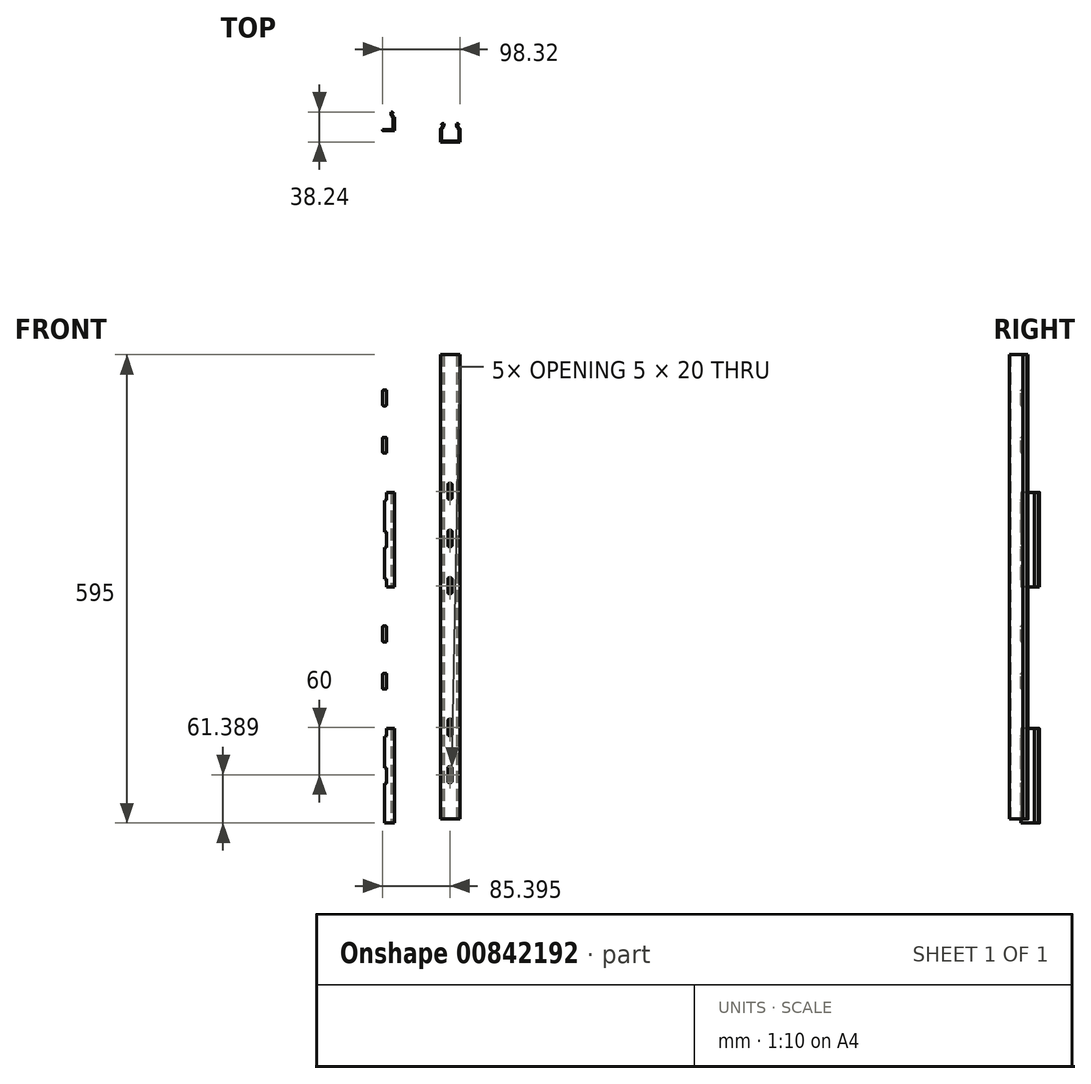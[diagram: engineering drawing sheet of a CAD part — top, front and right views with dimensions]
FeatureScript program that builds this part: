
annotation { "Feature Type Name" : "Feature", "Feature Type Description" : "" }
export const myFeature = defineFeature(function(context is Context, id is Id, definition is map)
    precondition{}
    {
        {
            var Q0;
            Q0=qCreatedBy(makeId("Top.planeOp"),FACE);
            var sketch = newSketch(context, id + "F0", { "sketchPlane" : qUnion([Q0])});
            skLineSegment(sketch, "E0", {"start": v(-70.87, 0) * mm, "end": v(-95.87, 0) * mm});
            skLineSegment(sketch, "E1", {"start": v(-95.87, 0) * mm, "end": v(-95.87, 17) * mm});
            skLineSegment(sketch, "E2", {"start": v(-83.37, 1.5) * mm, "end": v(-83.37, 14.96) * mm});
            skLineSegment(sketch, "E3", {"start": v(-94.37, 22) * mm, "end": v(-92.87, 22) * mm});
            skLineSegment(sketch, "E4.MirrorCS", {"start": v(-70.87, 0) * mm, "end": v(-70.87, 17) * mm});
            skPoint(sketch, "E5.orphan", {"position": v(-83.37, 0) * mm});
            skArc(sketch, "E6", {"start": v(-95.87, 17) * mm, "mid": v(-93.72, 19.11) * mm, "end": v(-92.87, 22) * mm});
            skLineSegment(sketch, "E7.1", {"start": v(-72.37, 1.5) * mm, "end": v(-72.37, 16.2) * mm});
            skLineSegment(sketch, "E7.2", {"start": v(-72.37, 1.5) * mm, "end": v(-94.37, 1.5) * mm});
            skLineSegment(sketch, "E7.3", {"start": v(-94.37, 1.5) * mm, "end": v(-94.37, 16.2) * mm});
            skArc(sketch, "E7.4", {"start": v(-94.37, 16.2) * mm, "mid": v(-91.9, 19.44) * mm, "end": v(-91.48, 23.5) * mm});
            skLineSegment(sketch, "E8.MirrorCS", {"start": v(-72.37, 22) * mm, "end": v(-73.87, 22) * mm});
            skArc(sketch, "E9.MirrorCS", {"start": v(-72.37, 16.2) * mm, "mid": v(-74.85, 19.44) * mm, "end": v(-75.26, 23.5) * mm});
            skArc(sketch, "E10.MirrorCS", {"start": v(-70.87, 17) * mm, "mid": v(-73.02, 19.11) * mm, "end": v(-73.87, 22) * mm});
            skArc(sketch, "E11", {"start": v(-91.48, 23.5) * mm, "mid": v(-93.28, 23.42) * mm, "end": v(-94.37, 22) * mm});
            skArc(sketch, "E12.MirrorCS", {"start": v(-75.26, 23.5) * mm, "mid": v(-73.47, 23.42) * mm, "end": v(-72.37, 22) * mm});
            skSolve(sketch);
        }
        {
            var Q0;
            {var subQ1=sQuery(id+"F0.wireOp",EDGE,"E0");Q0=makeQuery(id+"F0.imprint","IMPRINT",FACE,{"disambiguationData":[TD([[makeQuery(id+"F0.imprint","IMPRINT",EDGE,{"derivedFrom":subQ1}),-1.0]])]});}
            var Q1;
            Q1=makeQuery(id+"F0.imprint","IMPRINT",FACE,{"disambiguationData":[TD([[makeQuery(id+"F0.imprint","IMPRINT",EDGE,{"derivedFrom":sQuery(id+"F0.wireOp",EDGE,"8c0a88f1-b1bc-4309-b33d-9bf5d8da761c0.MirrorCS")}),-1.0]])]});
            var Q2;
            {var subQ5=sQuery(id+"F0.wireOp",EDGE,"E1");Q2=makeQuery(id+"F0.imprint","IMPRINT",FACE,{"disambiguationData":[TD([[makeQuery(id+"F0.imprint","IMPRINT",EDGE,{"derivedFrom":subQ5}),-1.0]])]});}
            var Q3;
            Q3=makeQuery(id+"F0.imprint","IMPRINT",FACE,{"disambiguationData":[TD([[makeQuery(id+"F0.imprint","IMPRINT",EDGE,{"derivedFrom":sQuery(id+"F0.wireOp",EDGE,"33b4dc04-297a-427e-952f-5a77545de1140.MirrorCS")}),-1.0]])]});
            extrude(context, id + "F1", {"entities" : qUnion([Q0, Q1, Q2, Q3]), "endBound" : BoundingType.SYMMETRIC, "depth" : 600 * mm, "offsetDistance" : 25 * mm});
        }
        {
            var Q0;
            Q0=makeQuery(id+"F1.opExtrude","SWEPT_FACE",FACE,{"disambiguationData":[OSD([sQuery(id+"F0.wireOp",EDGE,"E0")])]});
            var sketch = newSketch(context, id + "F2", { "sketchPlane" : qUnion([Q0])});
            skLineSegment(sketch, "E13", {"start": v(-83.37, -300) * mm, "end": v(-83.37, 300) * mm});
            skLineSegment(sketch, "E14.bottom", {"start": v(-81.87, 10) * mm, "end": v(-84.87, 10) * mm});
            skLineSegment(sketch, "E14.top", {"start": v(-81.87, -10) * mm, "end": v(-84.87, -10) * mm});
            skLineSegment(sketch, "E14.left", {"start": v(-80.87, 9) * mm, "end": v(-80.87, -9) * mm});
            skLineSegment(sketch, "E14.right", {"start": v(-85.87, 9) * mm, "end": v(-85.87, -9) * mm});
            skPoint(sketch, "E14.middle", {"position": v(-83.37, 0) * mm});
            skPoint(sketch, "E15.visualSharp", {"position": v(-85.87, -10) * mm});
            skArc(sketch, "E15.filletArc", {"start": v(-85.87, -9) * mm, "mid": v(-85.58, -9.7) * mm, "end": v(-84.87, -10) * mm});
            skPoint(sketch, "E16.visualSharp", {"position": v(-80.87, -10) * mm});
            skArc(sketch, "E16.filletArc", {"start": v(-81.87, -10) * mm, "mid": v(-81.16, -9.7) * mm, "end": v(-80.87, -9) * mm});
            skPoint(sketch, "E17.visualSharp", {"position": v(-85.87, 10) * mm});
            skArc(sketch, "E17.filletArc", {"start": v(-84.87, 10) * mm, "mid": v(-85.58, 9.7) * mm, "end": v(-85.87, 9) * mm});
            skPoint(sketch, "E18.visualSharp", {"position": v(-80.87, 10) * mm});
            skArc(sketch, "E18.filletArc", {"start": v(-80.87, 9) * mm, "mid": v(-81.16, 9.7) * mm, "end": v(-81.87, 10) * mm});
            skLineSegment(sketch, "E19.MirrorCS", {"start": v(-80.87, -69) * mm, "end": v(-80.87, -51) * mm});
            skLineSegment(sketch, "E20.MirrorCS", {"start": v(-81.87, -70) * mm, "end": v(-84.87, -70) * mm});
            skArc(sketch, "E21.MirrorCS", {"start": v(-80.87, -69) * mm, "mid": v(-81.16, -69.7) * mm, "end": v(-81.87, -70) * mm});
            skArc(sketch, "E22.MirrorCS", {"start": v(-84.87, -70) * mm, "mid": v(-85.58, -69.7) * mm, "end": v(-85.87, -69) * mm});
            skLineSegment(sketch, "E23.MirrorCS", {"start": v(-85.87, -69) * mm, "end": v(-85.87, -51) * mm});
            skArc(sketch, "E24.MirrorCS", {"start": v(-85.87, -51) * mm, "mid": v(-85.58, -50.3) * mm, "end": v(-84.87, -50) * mm});
            skLineSegment(sketch, "E25.MirrorCS", {"start": v(-81.87, -50) * mm, "end": v(-84.87, -50) * mm});
            skArc(sketch, "E26.MirrorCS", {"start": v(-81.87, -50) * mm, "mid": v(-81.16, -50.3) * mm, "end": v(-80.87, -51) * mm});
            skLineSegment(sketch, "E27", {"start": v(-83.37, 0) * mm, "end": v(-70.87, 0) * mm});
            skArc(sketch, "E28.MirrorCS", {"start": v(-84.87, 70) * mm, "mid": v(-85.58, 69.7) * mm, "end": v(-85.87, 69) * mm});
            skArc(sketch, "E29.MirrorCS", {"start": v(-85.87, 51) * mm, "mid": v(-85.58, 50.3) * mm, "end": v(-84.87, 50) * mm});
            skArc(sketch, "E30.MirrorCS", {"start": v(-80.87, 69) * mm, "mid": v(-81.16, 69.7) * mm, "end": v(-81.87, 70) * mm});
            skArc(sketch, "E31.MirrorCS", {"start": v(-81.87, 50) * mm, "mid": v(-81.16, 50.3) * mm, "end": v(-80.87, 51) * mm});
            skLineSegment(sketch, "E32.MirrorCS", {"start": v(-85.87, 69) * mm, "end": v(-85.87, 51) * mm});
            skLineSegment(sketch, "E33.MirrorCS", {"start": v(-81.87, 70) * mm, "end": v(-84.87, 70) * mm});
            skLineSegment(sketch, "E34.MirrorCS", {"start": v(-80.87, 69) * mm, "end": v(-80.87, 51) * mm});
            skLineSegment(sketch, "E35.MirrorCS", {"start": v(-81.87, 50) * mm, "end": v(-84.87, 50) * mm});
            skLineSegment(sketch, "E36", {"start": v(-83.37, -10) * mm, "end": v(-83.37, -50) * mm});
            skLineSegment(sketch, "E37", {"start": v(-85.87, -60) * mm, "end": v(-70.87, -60) * mm});
            skArc(sketch, "E38.MirrorCS", {"start": v(-81.87, -110) * mm, "mid": v(-81.16, -110.3) * mm, "end": v(-80.87, -111) * mm});
            skArc(sketch, "E39.MirrorCS", {"start": v(-84.87, -130) * mm, "mid": v(-85.58, -129.7) * mm, "end": v(-85.87, -129) * mm});
            skLineSegment(sketch, "E40.MirrorCS", {"start": v(-81.87, -110) * mm, "end": v(-84.87, -110) * mm});
            skArc(sketch, "E41.MirrorCS", {"start": v(-80.87, -129) * mm, "mid": v(-81.16, -129.7) * mm, "end": v(-81.87, -130) * mm});
            skLineSegment(sketch, "E42.MirrorCS", {"start": v(-81.87, -130) * mm, "end": v(-84.87, -130) * mm});
            skArc(sketch, "E43.MirrorCS", {"start": v(-85.87, -111) * mm, "mid": v(-85.58, -110.3) * mm, "end": v(-84.87, -110) * mm});
            skPoint(sketch, "E44.MirrorP", {"position": v(-80.87, -130) * mm});
            skPoint(sketch, "E45.MirrorP", {"position": v(-80.87, -110) * mm});
            skPoint(sketch, "E46.MirrorP", {"position": v(-85.87, -110) * mm});
            skLineSegment(sketch, "E47.MirrorCS", {"start": v(-83.37, -120) * mm, "end": v(-70.87, -120) * mm});
            skLineSegment(sketch, "E48.MirrorCS", {"start": v(-80.87, -129) * mm, "end": v(-80.87, -111) * mm});
            skPoint(sketch, "E49.MirrorP", {"position": v(-85.87, -130) * mm});
            skLineSegment(sketch, "E50.MirrorCS", {"start": v(-85.87, -129) * mm, "end": v(-85.87, -111) * mm});
            skPoint(sketch, "E51.MirrorP", {"position": v(-83.37, -120) * mm});
            skLineSegment(sketch, "E52.MirrorCS", {"start": v(-81.87, -190) * mm, "end": v(-84.87, -190) * mm});
            skArc(sketch, "E53.MirrorCS", {"start": v(-84.87, -170) * mm, "mid": v(-85.58, -170.3) * mm, "end": v(-85.87, -171) * mm});
            skArc(sketch, "E54.MirrorCS", {"start": v(-80.87, -171) * mm, "mid": v(-81.16, -170.3) * mm, "end": v(-81.87, -170) * mm});
            skLineSegment(sketch, "E55.MirrorCS", {"start": v(-81.87, -170) * mm, "end": v(-84.87, -170) * mm});
            skArc(sketch, "E56.MirrorCS", {"start": v(-85.87, -189) * mm, "mid": v(-85.58, -189.7) * mm, "end": v(-84.87, -190) * mm});
            skArc(sketch, "E57.MirrorCS", {"start": v(-81.87, -190) * mm, "mid": v(-81.16, -189.7) * mm, "end": v(-80.87, -189) * mm});
            skLineSegment(sketch, "E58.MirrorCS", {"start": v(-80.87, -171) * mm, "end": v(-80.87, -189) * mm});
            skLineSegment(sketch, "E59.MirrorCS", {"start": v(-85.87, -180) * mm, "end": v(-70.87, -180) * mm});
            skLineSegment(sketch, "E60.MirrorCS", {"start": v(-85.87, -171) * mm, "end": v(-85.87, -189) * mm});
            skLineSegment(sketch, "E61.MirrorCS", {"start": v(-81.87, -250) * mm, "end": v(-84.87, -250) * mm});
            skArc(sketch, "E62.MirrorCS", {"start": v(-84.87, -230) * mm, "mid": v(-85.58, -230.3) * mm, "end": v(-85.87, -231) * mm});
            skArc(sketch, "E63.MirrorCS", {"start": v(-85.87, -249) * mm, "mid": v(-85.58, -249.7) * mm, "end": v(-84.87, -250) * mm});
            skLineSegment(sketch, "E64.MirrorCS", {"start": v(-81.87, -230) * mm, "end": v(-84.87, -230) * mm});
            skArc(sketch, "E65.MirrorCS", {"start": v(-80.87, -231) * mm, "mid": v(-81.16, -230.3) * mm, "end": v(-81.87, -230) * mm});
            skArc(sketch, "E66.MirrorCS", {"start": v(-81.87, -250) * mm, "mid": v(-81.16, -249.7) * mm, "end": v(-80.87, -249) * mm});
            skPoint(sketch, "E67.MirrorP", {"position": v(-83.37, -240) * mm});
            skLineSegment(sketch, "E68.MirrorCS", {"start": v(-83.37, -240) * mm, "end": v(-70.87, -240) * mm});
            skPoint(sketch, "E69.MirrorP", {"position": v(-80.87, -230) * mm});
            skLineSegment(sketch, "E70.MirrorCS", {"start": v(-85.87, -231) * mm, "end": v(-85.87, -249) * mm});
            skPoint(sketch, "E71.MirrorP", {"position": v(-85.87, -230) * mm});
            skPoint(sketch, "E72.MirrorP", {"position": v(-85.87, -250) * mm});
            skLineSegment(sketch, "E73.MirrorCS", {"start": v(-80.87, -231) * mm, "end": v(-80.87, -249) * mm});
            skPoint(sketch, "E74.MirrorP", {"position": v(-80.87, -250) * mm});
            skArc(sketch, "E75.MirrorCS", {"start": v(-85.87, 249) * mm, "mid": v(-85.58, 249.7) * mm, "end": v(-84.87, 250) * mm});
            skLineSegment(sketch, "E76.MirrorCS", {"start": v(-81.87, 250) * mm, "end": v(-84.87, 250) * mm});
            skArc(sketch, "E77.MirrorCS", {"start": v(-81.87, 250) * mm, "mid": v(-81.16, 249.7) * mm, "end": v(-80.87, 249) * mm});
            skArc(sketch, "E78.MirrorCS", {"start": v(-80.87, 129) * mm, "mid": v(-81.16, 129.7) * mm, "end": v(-81.87, 130) * mm});
            skLineSegment(sketch, "E79.MirrorCS", {"start": v(-81.87, 130) * mm, "end": v(-84.87, 130) * mm});
            skArc(sketch, "E80.MirrorCS", {"start": v(-84.87, 130) * mm, "mid": v(-85.58, 129.7) * mm, "end": v(-85.87, 129) * mm});
            skArc(sketch, "E81.MirrorCS", {"start": v(-84.87, 230) * mm, "mid": v(-85.58, 230.3) * mm, "end": v(-85.87, 231) * mm});
            skLineSegment(sketch, "E82.MirrorCS", {"start": v(-81.87, 110) * mm, "end": v(-84.87, 110) * mm});
            skArc(sketch, "E83.MirrorCS", {"start": v(-85.87, 111) * mm, "mid": v(-85.58, 110.3) * mm, "end": v(-84.87, 110) * mm});
            skArc(sketch, "E84.MirrorCS", {"start": v(-81.87, 110) * mm, "mid": v(-81.16, 110.3) * mm, "end": v(-80.87, 111) * mm});
            skArc(sketch, "E85.MirrorCS", {"start": v(-80.87, 231) * mm, "mid": v(-81.16, 230.3) * mm, "end": v(-81.87, 230) * mm});
            skLineSegment(sketch, "E86.MirrorCS", {"start": v(-81.87, 230) * mm, "end": v(-84.87, 230) * mm});
            skArc(sketch, "E87.MirrorCS", {"start": v(-84.87, 170) * mm, "mid": v(-85.58, 170.3) * mm, "end": v(-85.87, 171) * mm});
            skArc(sketch, "E88.MirrorCS", {"start": v(-85.87, 189) * mm, "mid": v(-85.58, 189.7) * mm, "end": v(-84.87, 190) * mm});
            skLineSegment(sketch, "E89.MirrorCS", {"start": v(-81.87, 190) * mm, "end": v(-84.87, 190) * mm});
            skArc(sketch, "E90.MirrorCS", {"start": v(-80.87, 171) * mm, "mid": v(-81.16, 170.3) * mm, "end": v(-81.87, 170) * mm});
            skArc(sketch, "E91.MirrorCS", {"start": v(-81.87, 190) * mm, "mid": v(-81.16, 189.7) * mm, "end": v(-80.87, 189) * mm});
            skLineSegment(sketch, "E92.MirrorCS", {"start": v(-81.87, 170) * mm, "end": v(-84.87, 170) * mm});
            skLineSegment(sketch, "E93.MirrorCS", {"start": v(-85.87, 231) * mm, "end": v(-85.87, 249) * mm});
            skLineSegment(sketch, "E94.MirrorCS", {"start": v(-80.87, 129) * mm, "end": v(-80.87, 111) * mm});
            skLineSegment(sketch, "E95.MirrorCS", {"start": v(-85.87, 129) * mm, "end": v(-85.87, 111) * mm});
            skLineSegment(sketch, "E96.MirrorCS", {"start": v(-80.87, 231) * mm, "end": v(-80.87, 249) * mm});
            skPoint(sketch, "E97.MirrorP", {"position": v(-85.87, 230) * mm});
            skPoint(sketch, "E98.MirrorP", {"position": v(-80.87, 110) * mm});
            skPoint(sketch, "E99.MirrorP", {"position": v(-80.87, 230) * mm});
            skLineSegment(sketch, "E100.MirrorCS", {"start": v(-85.87, 171) * mm, "end": v(-85.87, 189) * mm});
            skLineSegment(sketch, "E101.MirrorCS", {"start": v(-83.37, 240) * mm, "end": v(-70.87, 240) * mm});
            skPoint(sketch, "E102.MirrorP", {"position": v(-80.87, 130) * mm});
            skPoint(sketch, "E103.MirrorP", {"position": v(-85.87, 250) * mm});
            skPoint(sketch, "E104.MirrorP", {"position": v(-83.37, 240) * mm});
            skLineSegment(sketch, "E105.MirrorCS", {"start": v(-80.87, 171) * mm, "end": v(-80.87, 189) * mm});
            skLineSegment(sketch, "E106.MirrorCS", {"start": v(-83.37, 120) * mm, "end": v(-70.87, 120) * mm});
            skPoint(sketch, "E107.MirrorP", {"position": v(-85.87, 110) * mm});
            skLineSegment(sketch, "E108.MirrorCS", {"start": v(-85.87, 180) * mm, "end": v(-70.87, 180) * mm});
            skPoint(sketch, "E109.MirrorP", {"position": v(-80.87, 250) * mm});
            skPoint(sketch, "E110.MirrorP", {"position": v(-83.37, 120) * mm});
            skPoint(sketch, "E111.MirrorP", {"position": v(-85.87, 130) * mm});
            skSolve(sketch);
        }
        {
            var Q0;
            Q0=makeQuery(id+"F2.imprint","IMPRINT",FACE,{"disambiguationData":[TD([[makeQuery(id+"F2.imprint","IMPRINT",EDGE,{"derivedFrom":sQuery(id+"F2.wireOp",EDGE,"E14.right")}),1.0]])]});
            var Q1;
            Q1=makeQuery(id+"F2.imprint","IMPRINT",FACE,{"disambiguationData":[TD([[makeQuery(id+"F2.imprint","IMPRINT",EDGE,{"derivedFrom":sQuery(id+"F2.wireOp",EDGE,"E14.left")}),-1.0]])]});
            var Q2;
            {var subQ0=sQuery(id+"F2.wireOp",EDGE,"E26.MirrorCS");Q2=makeQuery(id+"F2.imprint","IMPRINT",FACE,{"disambiguationData":[TD([[makeQuery(id+"F2.imprint","IMPRINT",EDGE,{"derivedFrom":subQ0}),-1.0]])]});}
            var Q3;
            {var subQ0=sQuery(id+"F2.wireOp",EDGE,"E21.MirrorCS");Q3=makeQuery(id+"F2.imprint","IMPRINT",FACE,{"disambiguationData":[TD([[makeQuery(id+"F2.imprint","IMPRINT",EDGE,{"derivedFrom":subQ0}),-1.0]])]});}
            var Q4;
            {var subQ0=sQuery(id+"F2.wireOp",EDGE,"E24.MirrorCS");Q4=makeQuery(id+"F2.imprint","IMPRINT",FACE,{"disambiguationData":[TD([[makeQuery(id+"F2.imprint","IMPRINT",EDGE,{"derivedFrom":subQ0}),-1.0]])]});}
            var Q5;
            {var subQ1=sQuery(id+"F2.wireOp",EDGE,"E22.MirrorCS");Q5=makeQuery(id+"F2.imprint","IMPRINT",FACE,{"disambiguationData":[TD([[makeQuery(id+"F2.imprint","IMPRINT",EDGE,{"derivedFrom":subQ1}),-1.0]])]});}
            var Q6;
            {var subQ5=sQuery(id+"F2.wireOp",EDGE,"E38.MirrorCS");Q6=makeQuery(id+"F2.imprint","IMPRINT",FACE,{"disambiguationData":[TD([[makeQuery(id+"F2.imprint","IMPRINT",EDGE,{"derivedFrom":subQ5}),-1.0]])]});}
            var Q7;
            {var subQ6=sQuery(id+"F2.wireOp",EDGE,"E41.MirrorCS");Q7=makeQuery(id+"F2.imprint","IMPRINT",FACE,{"disambiguationData":[TD([[makeQuery(id+"F2.imprint","IMPRINT",EDGE,{"derivedFrom":subQ6}),-1.0]])]});}
            var Q8;
            {var subQ5=sQuery(id+"F2.wireOp",EDGE,"E39.MirrorCS");Q8=makeQuery(id+"F2.imprint","IMPRINT",FACE,{"disambiguationData":[TD([[makeQuery(id+"F2.imprint","IMPRINT",EDGE,{"derivedFrom":subQ5}),-1.0]])]});}
            var Q9;
            {var subQ6=sQuery(id+"F2.wireOp",EDGE,"E53.MirrorCS");Q9=makeQuery(id+"F2.imprint","IMPRINT",FACE,{"disambiguationData":[TD([[makeQuery(id+"F2.imprint","IMPRINT",EDGE,{"derivedFrom":subQ6}),1.0]])]});}
            var Q10;
            {var subQ0=sQuery(id+"F2.wireOp",EDGE,"E56.MirrorCS");Q10=makeQuery(id+"F2.imprint","IMPRINT",FACE,{"disambiguationData":[TD([[makeQuery(id+"F2.imprint","IMPRINT",EDGE,{"derivedFrom":subQ0}),1.0]])]});}
            var Q11;
            {var subQ1=sQuery(id+"F2.wireOp",EDGE,"E57.MirrorCS");Q11=makeQuery(id+"F2.imprint","IMPRINT",FACE,{"disambiguationData":[TD([[makeQuery(id+"F2.imprint","IMPRINT",EDGE,{"derivedFrom":subQ1}),1.0]])]});}
            var Q12;
            {var subQ1=sQuery(id+"F2.wireOp",EDGE,"E54.MirrorCS");Q12=makeQuery(id+"F2.imprint","IMPRINT",FACE,{"disambiguationData":[TD([[makeQuery(id+"F2.imprint","IMPRINT",EDGE,{"derivedFrom":subQ1}),1.0]])]});}
            var Q13;
            {var subQ0=sQuery(id+"F2.wireOp",EDGE,"E62.MirrorCS");Q13=makeQuery(id+"F2.imprint","IMPRINT",FACE,{"disambiguationData":[TD([[makeQuery(id+"F2.imprint","IMPRINT",EDGE,{"derivedFrom":subQ0}),1.0]])]});}
            var Q14;
            {var subQ5=sQuery(id+"F2.wireOp",EDGE,"E65.MirrorCS");Q14=makeQuery(id+"F2.imprint","IMPRINT",FACE,{"disambiguationData":[TD([[makeQuery(id+"F2.imprint","IMPRINT",EDGE,{"derivedFrom":subQ5}),1.0]])]});}
            var Q15;
            {var subQ7=sQuery(id+"F2.wireOp",EDGE,"E66.MirrorCS");Q15=makeQuery(id+"F2.imprint","IMPRINT",FACE,{"disambiguationData":[TD([[makeQuery(id+"F2.imprint","IMPRINT",EDGE,{"derivedFrom":subQ7}),1.0]])]});}
            var Q16;
            {var subQ1=sQuery(id+"F2.wireOp",EDGE,"E30.MirrorCS");Q16=makeQuery(id+"F2.imprint","IMPRINT",FACE,{"disambiguationData":[TD([[makeQuery(id+"F2.imprint","IMPRINT",EDGE,{"derivedFrom":subQ1}),1.0]])]});}
            var Q17;
            {var subQ1=sQuery(id+"F2.wireOp",EDGE,"E28.MirrorCS");Q17=makeQuery(id+"F2.imprint","IMPRINT",FACE,{"disambiguationData":[TD([[makeQuery(id+"F2.imprint","IMPRINT",EDGE,{"derivedFrom":subQ1}),1.0]])]});}
            var Q18;
            {var subQ1=sQuery(id+"F2.wireOp",EDGE,"E78.MirrorCS");Q18=makeQuery(id+"F2.imprint","IMPRINT",FACE,{"disambiguationData":[TD([[makeQuery(id+"F2.imprint","IMPRINT",EDGE,{"derivedFrom":subQ1}),1.0]])]});}
            var Q19;
            {var subQ1=sQuery(id+"F2.wireOp",EDGE,"E84.MirrorCS");Q19=makeQuery(id+"F2.imprint","IMPRINT",FACE,{"disambiguationData":[TD([[makeQuery(id+"F2.imprint","IMPRINT",EDGE,{"derivedFrom":subQ1}),1.0]])]});}
            var Q20;
            {var subQ0=sQuery(id+"F2.wireOp",EDGE,"E80.MirrorCS");Q20=makeQuery(id+"F2.imprint","IMPRINT",FACE,{"disambiguationData":[TD([[makeQuery(id+"F2.imprint","IMPRINT",EDGE,{"derivedFrom":subQ0}),1.0]])]});}
            var Q21;
            {var subQ1=sQuery(id+"F2.wireOp",EDGE,"E91.MirrorCS");Q21=makeQuery(id+"F2.imprint","IMPRINT",FACE,{"disambiguationData":[TD([[makeQuery(id+"F2.imprint","IMPRINT",EDGE,{"derivedFrom":subQ1}),-1.0]])]});}
            var Q22;
            {var subQ1=sQuery(id+"F2.wireOp",EDGE,"E90.MirrorCS");Q22=makeQuery(id+"F2.imprint","IMPRINT",FACE,{"disambiguationData":[TD([[makeQuery(id+"F2.imprint","IMPRINT",EDGE,{"derivedFrom":subQ1}),-1.0]])]});}
            var Q23;
            {var subQ1=sQuery(id+"F2.wireOp",EDGE,"E87.MirrorCS");Q23=makeQuery(id+"F2.imprint","IMPRINT",FACE,{"disambiguationData":[TD([[makeQuery(id+"F2.imprint","IMPRINT",EDGE,{"derivedFrom":subQ1}),-1.0]])]});}
            var Q24;
            {var subQ1=sQuery(id+"F2.wireOp",EDGE,"E88.MirrorCS");Q24=makeQuery(id+"F2.imprint","IMPRINT",FACE,{"disambiguationData":[TD([[makeQuery(id+"F2.imprint","IMPRINT",EDGE,{"derivedFrom":subQ1}),-1.0]])]});}
            var Q25;
            {var subQ0=sQuery(id+"F2.wireOp",EDGE,"E77.MirrorCS");Q25=makeQuery(id+"F2.imprint","IMPRINT",FACE,{"disambiguationData":[TD([[makeQuery(id+"F2.imprint","IMPRINT",EDGE,{"derivedFrom":subQ0}),-1.0]])]});}
            var Q26;
            {var subQ1=sQuery(id+"F2.wireOp",EDGE,"E85.MirrorCS");Q26=makeQuery(id+"F2.imprint","IMPRINT",FACE,{"disambiguationData":[TD([[makeQuery(id+"F2.imprint","IMPRINT",EDGE,{"derivedFrom":subQ1}),-1.0]])]});}
            var Q27;
            {var subQ3=sQuery(id+"F2.wireOp",EDGE,"E75.MirrorCS");Q27=makeQuery(id+"F2.imprint","IMPRINT",FACE,{"disambiguationData":[TD([[makeQuery(id+"F2.imprint","IMPRINT",EDGE,{"derivedFrom":subQ3}),-1.0]])]});}
            extrude(context, id + "F3", {"entities" : qUnion([Q0, Q1, Q2, Q3, Q4, Q5, Q6, Q7, Q8, Q9, Q10, Q11, Q12, Q13, Q14, Q15, Q16, Q17, Q18, Q19, Q20, Q21, Q22, Q23, Q24, Q25, Q26, Q27]), "operationType" : NewBodyOperationType.REMOVE, "oppositeDirection" : true, "depth" : 25 * mm, "offsetDistance" : 25 * mm});
        }
        {
            var Q0;
            Q0=qCreatedBy(makeId("Top.planeOp"),FACE);
            var sketch = newSketch(context, id + "F4", { "sketchPlane" : qUnion([Q0])});
            skLineSegment(sketch, "E112", {"start": v(12.45, -14.58) * mm, "end": v(-12.55, -14.58) * mm});
            skLineSegment(sketch, "E113", {"start": v(-12.55, -14.58) * mm, "end": v(-12.55, 2.42) * mm});
            skLineSegment(sketch, "E114", {"start": v(-11.05, 7.42) * mm, "end": v(-9.55, 7.42) * mm});
            skLineSegment(sketch, "E115.3", {"start": v(10.95, -13.08) * mm, "end": v(-11.05, -13.08) * mm});
            skLineSegment(sketch, "E116.MirrorCS", {"start": v(12.45, -14.58) * mm, "end": v(12.45, 2.42) * mm});
            skPoint(sketch, "E117.start.orphan", {"position": v(-0.05, -14.58) * mm});
            skArc(sketch, "E118", {"start": v(-12.55, 2.42) * mm, "mid": v(-10.4, 4.53) * mm, "end": v(-9.55, 7.42) * mm});
            skArc(sketch, "E119.1", {"start": v(-11.05, 1.61) * mm, "mid": v(-8.58, 4.85) * mm, "end": v(-8.16, 8.92) * mm});
            skLineSegment(sketch, "E119.2", {"start": v(-11.05, -13.08) * mm, "end": v(-11.05, 1.61) * mm});
            skArc(sketch, "E120", {"start": v(-8.16, 8.92) * mm, "mid": v(-9.96, 8.84) * mm, "end": v(-11.05, 7.42) * mm});
            skLineSegment(sketch, "E121.MirrorCS", {"start": v(10.95, 7.42) * mm, "end": v(9.45, 7.42) * mm});
            skArc(sketch, "E122.MirrorCS", {"start": v(8.06, 8.92) * mm, "mid": v(9.85, 8.84) * mm, "end": v(10.95, 7.42) * mm});
            skArc(sketch, "E123.MirrorCS", {"start": v(10.95, 1.61) * mm, "mid": v(8.47, 4.85) * mm, "end": v(8.06, 8.92) * mm});
            skArc(sketch, "E124.MirrorCS", {"start": v(12.45, 2.42) * mm, "mid": v(10.3, 4.53) * mm, "end": v(9.45, 7.42) * mm});
            skLineSegment(sketch, "E125.MirrorCS", {"start": v(10.95, -13.08) * mm, "end": v(10.95, 1.61) * mm});
            skPoint(sketch, "E126.orphan", {"position": v(-11.05, -14.58) * mm});
            skPoint(sketch, "E127.orphan", {"position": v(10.95, -14.58) * mm});
            skSolve(sketch);
        }
        {
            var Q0;
            {var subQ1=sQuery(id+"F4.wireOp",EDGE,"E112");Q0=makeQuery(id+"F4.imprint","IMPRINT",FACE,{"disambiguationData":[TD([[makeQuery(id+"F4.imprint","IMPRINT",EDGE,{"derivedFrom":subQ1}),-1.0]])]});}
            var Q1;
            Q1=makeQuery(id+"F4.imprint","IMPRINT",FACE,{"disambiguationData":[TD([[makeQuery(id+"F4.imprint","IMPRINT",EDGE,{"derivedFrom":sQuery(id+"F4.wireOp",EDGE,"5638b72b-f4fd-4419-a1c8-03f46051a929.MirrorCS")}),-1.0]])]});
            extrude(context, id + "F5", {"entities" : qUnion([Q0, Q1]), "endBound" : BoundingType.SYMMETRIC, "depth" : 590 * mm, "offsetDistance" : 25 * mm});
        }
        {
            var Q0;
            Q0=qCreatedBy(makeId("Front.planeOp"),FACE);
            var sketch = newSketch(context, id + "F6", { "sketchPlane" : qUnion([Q0])});
            skLineSegment(sketch, "E128", {"start": v(-0.47, -248.61) * mm, "end": v(-0.47, 251.39) * mm});
            skLineSegment(sketch, "E129.bottom", {"start": v(1.03, 11.39) * mm, "end": v(-1.97, 11.39) * mm});
            skLineSegment(sketch, "E129.top", {"start": v(1.03, -8.61) * mm, "end": v(-1.97, -8.61) * mm});
            skLineSegment(sketch, "E129.left", {"start": v(2.03, 10.39) * mm, "end": v(2.03, -7.61) * mm});
            skLineSegment(sketch, "E129.right", {"start": v(-2.97, 10.39) * mm, "end": v(-2.97, -7.61) * mm});
            skPoint(sketch, "E129.middle", {"position": v(-0.47, 1.39) * mm});
            skPoint(sketch, "E130.visualSharp", {"position": v(-2.97, -8.61) * mm});
            skArc(sketch, "E130.filletArc", {"start": v(-2.97, -7.61) * mm, "mid": v(-2.68, -8.32) * mm, "end": v(-1.97, -8.61) * mm});
            skPoint(sketch, "E131.visualSharp", {"position": v(2.03, -8.61) * mm});
            skArc(sketch, "E131.filletArc", {"start": v(1.03, -8.61) * mm, "mid": v(1.73, -8.32) * mm, "end": v(2.03, -7.61) * mm});
            skPoint(sketch, "E132.visualSharp", {"position": v(-2.97, 11.39) * mm});
            skArc(sketch, "E132.filletArc", {"start": v(-1.97, 11.39) * mm, "mid": v(-2.68, 11.1) * mm, "end": v(-2.97, 10.39) * mm});
            skPoint(sketch, "E133.visualSharp", {"position": v(2.03, 11.39) * mm});
            skArc(sketch, "E133.filletArc", {"start": v(2.03, 10.39) * mm, "mid": v(1.73, 11.1) * mm, "end": v(1.03, 11.39) * mm});
            skLineSegment(sketch, "E134.MirrorCS", {"start": v(2.03, -67.61) * mm, "end": v(2.03, -49.61) * mm});
            skLineSegment(sketch, "E135.MirrorCS", {"start": v(1.03, -68.61) * mm, "end": v(-1.97, -68.61) * mm});
            skArc(sketch, "E136.MirrorCS", {"start": v(2.03, -67.61) * mm, "mid": v(1.73, -68.32) * mm, "end": v(1.03, -68.61) * mm});
            skArc(sketch, "E137.MirrorCS", {"start": v(-1.97, -68.61) * mm, "mid": v(-2.68, -68.32) * mm, "end": v(-2.97, -67.61) * mm});
            skLineSegment(sketch, "E138.MirrorCS", {"start": v(-2.97, -67.61) * mm, "end": v(-2.97, -49.61) * mm});
            skArc(sketch, "E139.MirrorCS", {"start": v(-2.97, -49.61) * mm, "mid": v(-2.68, -48.9) * mm, "end": v(-1.97, -48.61) * mm});
            skLineSegment(sketch, "E140.MirrorCS", {"start": v(1.03, -48.61) * mm, "end": v(-1.97, -48.61) * mm});
            skArc(sketch, "E141.MirrorCS", {"start": v(1.03, -48.61) * mm, "mid": v(1.73, -48.9) * mm, "end": v(2.03, -49.61) * mm});
            skLineSegment(sketch, "E142", {"start": v(-0.47, 1.39) * mm, "end": v(12.03, 1.39) * mm});
            skArc(sketch, "E143.MirrorCS", {"start": v(-1.97, 71.39) * mm, "mid": v(-2.68, 71.1) * mm, "end": v(-2.97, 70.39) * mm});
            skArc(sketch, "E144.MirrorCS", {"start": v(-2.97, 52.39) * mm, "mid": v(-2.68, 51.68) * mm, "end": v(-1.97, 51.39) * mm});
            skArc(sketch, "E145.MirrorCS", {"start": v(2.03, 70.39) * mm, "mid": v(1.73, 71.1) * mm, "end": v(1.03, 71.39) * mm});
            skArc(sketch, "E146.MirrorCS", {"start": v(1.03, 51.39) * mm, "mid": v(1.73, 51.68) * mm, "end": v(2.03, 52.39) * mm});
            skLineSegment(sketch, "E147.MirrorCS", {"start": v(-2.97, 70.39) * mm, "end": v(-2.97, 52.39) * mm});
            skLineSegment(sketch, "E148.MirrorCS", {"start": v(1.03, 71.39) * mm, "end": v(-1.97, 71.39) * mm});
            skLineSegment(sketch, "E149.MirrorCS", {"start": v(2.03, 70.39) * mm, "end": v(2.03, 52.39) * mm});
            skLineSegment(sketch, "E150.MirrorCS", {"start": v(1.03, 51.39) * mm, "end": v(-1.97, 51.39) * mm});
            skLineSegment(sketch, "E151", {"start": v(-0.47, -8.61) * mm, "end": v(-0.47, -48.61) * mm});
            skLineSegment(sketch, "E152", {"start": v(-2.97, -58.61) * mm, "end": v(12.03, -58.61) * mm});
            skArc(sketch, "E153.MirrorCS", {"start": v(1.03, -108.61) * mm, "mid": v(1.73, -108.9) * mm, "end": v(2.03, -109.61) * mm});
            skArc(sketch, "E154.MirrorCS", {"start": v(-1.97, -128.61) * mm, "mid": v(-2.68, -128.32) * mm, "end": v(-2.97, -127.61) * mm});
            skLineSegment(sketch, "E155.MirrorCS", {"start": v(1.03, -108.61) * mm, "end": v(-1.97, -108.61) * mm});
            skArc(sketch, "E156.MirrorCS", {"start": v(2.03, -127.61) * mm, "mid": v(1.73, -128.32) * mm, "end": v(1.03, -128.61) * mm});
            skLineSegment(sketch, "E157.MirrorCS", {"start": v(1.03, -128.61) * mm, "end": v(-1.97, -128.61) * mm});
            skArc(sketch, "E158.MirrorCS", {"start": v(-2.97, -109.61) * mm, "mid": v(-2.68, -108.9) * mm, "end": v(-1.97, -108.61) * mm});
            skPoint(sketch, "E159.MirrorP", {"position": v(2.03, -128.61) * mm});
            skPoint(sketch, "E160.MirrorP", {"position": v(2.03, -108.61) * mm});
            skPoint(sketch, "E161.MirrorP", {"position": v(-2.97, -108.61) * mm});
            skLineSegment(sketch, "E162.MirrorCS", {"start": v(-0.47, -118.61) * mm, "end": v(12.03, -118.61) * mm});
            skLineSegment(sketch, "E163.MirrorCS", {"start": v(2.03, -127.61) * mm, "end": v(2.03, -109.61) * mm});
            skPoint(sketch, "E164.MirrorP", {"position": v(-2.97, -128.61) * mm});
            skLineSegment(sketch, "E165.MirrorCS", {"start": v(-2.97, -127.61) * mm, "end": v(-2.97, -109.61) * mm});
            skPoint(sketch, "E166.MirrorP", {"position": v(-0.47, -118.61) * mm});
            skLineSegment(sketch, "E167.MirrorCS", {"start": v(1.03, -188.61) * mm, "end": v(-1.97, -188.61) * mm});
            skArc(sketch, "E168.MirrorCS", {"start": v(-1.97, -168.61) * mm, "mid": v(-2.68, -168.9) * mm, "end": v(-2.97, -169.61) * mm});
            skArc(sketch, "E169.MirrorCS", {"start": v(2.03, -169.61) * mm, "mid": v(1.73, -168.9) * mm, "end": v(1.03, -168.61) * mm});
            skLineSegment(sketch, "E170.MirrorCS", {"start": v(1.03, -168.61) * mm, "end": v(-1.97, -168.61) * mm});
            skArc(sketch, "E171.MirrorCS", {"start": v(-2.97, -187.61) * mm, "mid": v(-2.68, -188.32) * mm, "end": v(-1.97, -188.61) * mm});
            skArc(sketch, "E172.MirrorCS", {"start": v(1.03, -188.61) * mm, "mid": v(1.73, -188.32) * mm, "end": v(2.03, -187.61) * mm});
            skLineSegment(sketch, "E173.MirrorCS", {"start": v(2.03, -169.61) * mm, "end": v(2.03, -187.61) * mm});
            skLineSegment(sketch, "E174.MirrorCS", {"start": v(-2.97, -178.61) * mm, "end": v(12.03, -178.61) * mm});
            skLineSegment(sketch, "E175.MirrorCS", {"start": v(-2.97, -169.61) * mm, "end": v(-2.97, -187.61) * mm});
            skLineSegment(sketch, "E176.MirrorCS", {"start": v(1.03, -248.61) * mm, "end": v(-1.97, -248.61) * mm});
            skArc(sketch, "E177.MirrorCS", {"start": v(-1.97, -228.61) * mm, "mid": v(-2.68, -228.9) * mm, "end": v(-2.97, -229.61) * mm});
            skArc(sketch, "E178.MirrorCS", {"start": v(-2.97, -247.61) * mm, "mid": v(-2.68, -248.32) * mm, "end": v(-1.97, -248.61) * mm});
            skLineSegment(sketch, "E179.MirrorCS", {"start": v(1.03, -228.61) * mm, "end": v(-1.97, -228.61) * mm});
            skArc(sketch, "E180.MirrorCS", {"start": v(2.03, -229.61) * mm, "mid": v(1.73, -228.9) * mm, "end": v(1.03, -228.61) * mm});
            skArc(sketch, "E181.MirrorCS", {"start": v(1.03, -248.61) * mm, "mid": v(1.73, -248.32) * mm, "end": v(2.03, -247.61) * mm});
            skPoint(sketch, "E182.MirrorP", {"position": v(-0.47, -238.61) * mm});
            skLineSegment(sketch, "E183.MirrorCS", {"start": v(-0.47, -238.61) * mm, "end": v(12.03, -238.61) * mm});
            skPoint(sketch, "E184.MirrorP", {"position": v(2.03, -228.61) * mm});
            skLineSegment(sketch, "E185.MirrorCS", {"start": v(-2.97, -229.61) * mm, "end": v(-2.97, -247.61) * mm});
            skPoint(sketch, "E186.MirrorP", {"position": v(-2.97, -228.61) * mm});
            skPoint(sketch, "E187.MirrorP", {"position": v(-2.97, -248.61) * mm});
            skLineSegment(sketch, "E188.MirrorCS", {"start": v(2.03, -229.61) * mm, "end": v(2.03, -247.61) * mm});
            skPoint(sketch, "E189.MirrorP", {"position": v(2.03, -248.61) * mm});
            skArc(sketch, "E190.MirrorCS", {"start": v(-2.97, 250.39) * mm, "mid": v(-2.68, 251.1) * mm, "end": v(-1.97, 251.39) * mm});
            skLineSegment(sketch, "E191.MirrorCS", {"start": v(1.03, 251.39) * mm, "end": v(-1.97, 251.39) * mm});
            skArc(sketch, "E192.MirrorCS", {"start": v(1.03, 251.39) * mm, "mid": v(1.73, 251.1) * mm, "end": v(2.03, 250.39) * mm});
            skArc(sketch, "E193.MirrorCS", {"start": v(2.03, 130.39) * mm, "mid": v(1.73, 131.1) * mm, "end": v(1.03, 131.39) * mm});
            skLineSegment(sketch, "E194.MirrorCS", {"start": v(1.03, 131.39) * mm, "end": v(-1.97, 131.39) * mm});
            skArc(sketch, "E195.MirrorCS", {"start": v(-1.97, 131.39) * mm, "mid": v(-2.68, 131.1) * mm, "end": v(-2.97, 130.39) * mm});
            skArc(sketch, "E196.MirrorCS", {"start": v(-1.97, 231.39) * mm, "mid": v(-2.68, 231.68) * mm, "end": v(-2.97, 232.39) * mm});
            skLineSegment(sketch, "E197.MirrorCS", {"start": v(1.03, 111.39) * mm, "end": v(-1.97, 111.39) * mm});
            skArc(sketch, "E198.MirrorCS", {"start": v(-2.97, 112.39) * mm, "mid": v(-2.68, 111.68) * mm, "end": v(-1.97, 111.39) * mm});
            skArc(sketch, "E199.MirrorCS", {"start": v(1.03, 111.39) * mm, "mid": v(1.73, 111.68) * mm, "end": v(2.03, 112.39) * mm});
            skArc(sketch, "E200.MirrorCS", {"start": v(2.03, 232.39) * mm, "mid": v(1.73, 231.68) * mm, "end": v(1.03, 231.39) * mm});
            skLineSegment(sketch, "E201.MirrorCS", {"start": v(1.03, 231.39) * mm, "end": v(-1.97, 231.39) * mm});
            skArc(sketch, "E202.MirrorCS", {"start": v(-1.97, 171.39) * mm, "mid": v(-2.68, 171.68) * mm, "end": v(-2.97, 172.39) * mm});
            skArc(sketch, "E203.MirrorCS", {"start": v(-2.97, 190.39) * mm, "mid": v(-2.68, 191.1) * mm, "end": v(-1.97, 191.39) * mm});
            skLineSegment(sketch, "E204.MirrorCS", {"start": v(1.03, 191.39) * mm, "end": v(-1.97, 191.39) * mm});
            skArc(sketch, "E205.MirrorCS", {"start": v(2.03, 172.39) * mm, "mid": v(1.73, 171.68) * mm, "end": v(1.03, 171.39) * mm});
            skArc(sketch, "E206.MirrorCS", {"start": v(1.03, 191.39) * mm, "mid": v(1.73, 191.1) * mm, "end": v(2.03, 190.39) * mm});
            skLineSegment(sketch, "E207.MirrorCS", {"start": v(1.03, 171.39) * mm, "end": v(-1.97, 171.39) * mm});
            skLineSegment(sketch, "E208.MirrorCS", {"start": v(-2.97, 232.39) * mm, "end": v(-2.97, 250.39) * mm});
            skLineSegment(sketch, "E209.MirrorCS", {"start": v(2.03, 130.39) * mm, "end": v(2.03, 112.39) * mm});
            skLineSegment(sketch, "E210.MirrorCS", {"start": v(-2.97, 130.39) * mm, "end": v(-2.97, 112.39) * mm});
            skLineSegment(sketch, "E211.MirrorCS", {"start": v(2.03, 232.39) * mm, "end": v(2.03, 250.39) * mm});
            skPoint(sketch, "E212.MirrorP", {"position": v(-2.97, 231.39) * mm});
            skPoint(sketch, "E213.MirrorP", {"position": v(2.03, 111.39) * mm});
            skPoint(sketch, "E214.MirrorP", {"position": v(2.03, 231.39) * mm});
            skLineSegment(sketch, "E215.MirrorCS", {"start": v(-2.97, 172.39) * mm, "end": v(-2.97, 190.39) * mm});
            skLineSegment(sketch, "E216.MirrorCS", {"start": v(-0.47, 241.39) * mm, "end": v(12.03, 241.39) * mm});
            skPoint(sketch, "E217.MirrorP", {"position": v(2.03, 131.39) * mm});
            skPoint(sketch, "E218.MirrorP", {"position": v(-2.97, 251.39) * mm});
            skPoint(sketch, "E219.MirrorP", {"position": v(-0.47, 241.39) * mm});
            skLineSegment(sketch, "E220.MirrorCS", {"start": v(2.03, 172.39) * mm, "end": v(2.03, 190.39) * mm});
            skLineSegment(sketch, "E221.MirrorCS", {"start": v(-0.47, 121.39) * mm, "end": v(12.03, 121.39) * mm});
            skPoint(sketch, "E222.MirrorP", {"position": v(-2.97, 111.39) * mm});
            skLineSegment(sketch, "E223.MirrorCS", {"start": v(-2.97, 181.39) * mm, "end": v(12.03, 181.39) * mm});
            skPoint(sketch, "E224.MirrorP", {"position": v(2.03, 251.39) * mm});
            skPoint(sketch, "E225.MirrorP", {"position": v(-0.47, 121.39) * mm});
            skPoint(sketch, "E226.MirrorP", {"position": v(-2.97, 131.39) * mm});
            skSolve(sketch);
        }
        {
            var Q0;
            {var subQ0=sQuery(id+"F6.wireOp",EDGE,"E177.MirrorCS");Q0=makeQuery(id+"F6.imprint","IMPRINT",FACE,{"disambiguationData":[TD([[makeQuery(id+"F6.imprint","IMPRINT",EDGE,{"derivedFrom":subQ0}),1.0]])]});}
            var Q1;
            {var subQ5=sQuery(id+"F6.wireOp",EDGE,"E180.MirrorCS");Q1=makeQuery(id+"F6.imprint","IMPRINT",FACE,{"disambiguationData":[TD([[makeQuery(id+"F6.imprint","IMPRINT",EDGE,{"derivedFrom":subQ5}),1.0]])]});}
            var Q2;
            {var subQ5=sQuery(id+"F6.wireOp",EDGE,"E181.MirrorCS");Q2=makeQuery(id+"F6.imprint","IMPRINT",FACE,{"disambiguationData":[TD([[makeQuery(id+"F6.imprint","IMPRINT",EDGE,{"derivedFrom":subQ5}),1.0]])]});}
            var Q3;
            {var subQ1=sQuery(id+"F6.wireOp",EDGE,"E169.MirrorCS");Q3=makeQuery(id+"F6.imprint","IMPRINT",FACE,{"disambiguationData":[TD([[makeQuery(id+"F6.imprint","IMPRINT",EDGE,{"derivedFrom":subQ1}),1.0]])]});}
            var Q4;
            {var subQ0=sQuery(id+"F6.wireOp",EDGE,"E168.MirrorCS");Q4=makeQuery(id+"F6.imprint","IMPRINT",FACE,{"disambiguationData":[TD([[makeQuery(id+"F6.imprint","IMPRINT",EDGE,{"derivedFrom":subQ0}),1.0]])]});}
            var Q5;
            {var subQ5=sQuery(id+"F6.wireOp",EDGE,"E171.MirrorCS");Q5=makeQuery(id+"F6.imprint","IMPRINT",FACE,{"disambiguationData":[TD([[makeQuery(id+"F6.imprint","IMPRINT",EDGE,{"derivedFrom":subQ5}),1.0]])]});}
            var Q6;
            {var subQ0=sQuery(id+"F6.wireOp",EDGE,"E172.MirrorCS");Q6=makeQuery(id+"F6.imprint","IMPRINT",FACE,{"disambiguationData":[TD([[makeQuery(id+"F6.imprint","IMPRINT",EDGE,{"derivedFrom":subQ0}),1.0]])]});}
            var Q7;
            {var subQ0=sQuery(id+"F6.wireOp",EDGE,"E154.MirrorCS");Q7=makeQuery(id+"F6.imprint","IMPRINT",FACE,{"disambiguationData":[TD([[makeQuery(id+"F6.imprint","IMPRINT",EDGE,{"derivedFrom":subQ0}),-1.0]])]});}
            var Q8;
            {var subQ6=sQuery(id+"F6.wireOp",EDGE,"E153.MirrorCS");Q8=makeQuery(id+"F6.imprint","IMPRINT",FACE,{"disambiguationData":[TD([[makeQuery(id+"F6.imprint","IMPRINT",EDGE,{"derivedFrom":subQ6}),-1.0]])]});}
            var Q9;
            {var subQ1=sQuery(id+"F6.wireOp",EDGE,"E156.MirrorCS");Q9=makeQuery(id+"F6.imprint","IMPRINT",FACE,{"disambiguationData":[TD([[makeQuery(id+"F6.imprint","IMPRINT",EDGE,{"derivedFrom":subQ1}),-1.0]])]});}
            var Q10;
            {var subQ1=sQuery(id+"F6.wireOp",EDGE,"E139.MirrorCS");Q10=makeQuery(id+"F6.imprint","IMPRINT",FACE,{"disambiguationData":[TD([[makeQuery(id+"F6.imprint","IMPRINT",EDGE,{"derivedFrom":subQ1}),-1.0]])]});}
            var Q11;
            {var subQ0=sQuery(id+"F6.wireOp",EDGE,"E141.MirrorCS");Q11=makeQuery(id+"F6.imprint","IMPRINT",FACE,{"disambiguationData":[TD([[makeQuery(id+"F6.imprint","IMPRINT",EDGE,{"derivedFrom":subQ0}),-1.0]])]});}
            var Q12;
            {var subQ0=sQuery(id+"F6.wireOp",EDGE,"E136.MirrorCS");Q12=makeQuery(id+"F6.imprint","IMPRINT",FACE,{"disambiguationData":[TD([[makeQuery(id+"F6.imprint","IMPRINT",EDGE,{"derivedFrom":subQ0}),-1.0]])]});}
            var Q13;
            {var subQ1=sQuery(id+"F6.wireOp",EDGE,"E137.MirrorCS");Q13=makeQuery(id+"F6.imprint","IMPRINT",FACE,{"disambiguationData":[TD([[makeQuery(id+"F6.imprint","IMPRINT",EDGE,{"derivedFrom":subQ1}),-1.0]])]});}
            var Q14;
            Q14=makeQuery(id+"F6.imprint","IMPRINT",FACE,{"disambiguationData":[TD([[makeQuery(id+"F6.imprint","IMPRINT",EDGE,{"derivedFrom":sQuery(id+"F6.wireOp",EDGE,"E129.right")}),1.0]])]});
            var Q15;
            {var subQ0=sQuery(id+"F6.wireOp",EDGE,"E133.filletArc");Q15=makeQuery(id+"F6.imprint","IMPRINT",FACE,{"disambiguationData":[TD([[makeQuery(id+"F6.imprint","IMPRINT",EDGE,{"derivedFrom":subQ0}),1.0]])]});}
            var Q16;
            {var subQ0=sQuery(id+"F6.wireOp",EDGE,"E131.filletArc");Q16=makeQuery(id+"F6.imprint","IMPRINT",FACE,{"disambiguationData":[TD([[makeQuery(id+"F6.imprint","IMPRINT",EDGE,{"derivedFrom":subQ0}),1.0]])]});}
            var Q17;
            {var subQ1=sQuery(id+"F6.wireOp",EDGE,"E143.MirrorCS");Q17=makeQuery(id+"F6.imprint","IMPRINT",FACE,{"disambiguationData":[TD([[makeQuery(id+"F6.imprint","IMPRINT",EDGE,{"derivedFrom":subQ1}),1.0]])]});}
            var Q18;
            {var subQ1=sQuery(id+"F6.wireOp",EDGE,"E145.MirrorCS");Q18=makeQuery(id+"F6.imprint","IMPRINT",FACE,{"disambiguationData":[TD([[makeQuery(id+"F6.imprint","IMPRINT",EDGE,{"derivedFrom":subQ1}),1.0]])]});}
            var Q19;
            {var subQ0=sQuery(id+"F6.wireOp",EDGE,"E195.MirrorCS");Q19=makeQuery(id+"F6.imprint","IMPRINT",FACE,{"disambiguationData":[TD([[makeQuery(id+"F6.imprint","IMPRINT",EDGE,{"derivedFrom":subQ0}),1.0]])]});}
            var Q20;
            {var subQ1=sQuery(id+"F6.wireOp",EDGE,"E193.MirrorCS");Q20=makeQuery(id+"F6.imprint","IMPRINT",FACE,{"disambiguationData":[TD([[makeQuery(id+"F6.imprint","IMPRINT",EDGE,{"derivedFrom":subQ1}),1.0]])]});}
            var Q21;
            {var subQ1=sQuery(id+"F6.wireOp",EDGE,"E199.MirrorCS");Q21=makeQuery(id+"F6.imprint","IMPRINT",FACE,{"disambiguationData":[TD([[makeQuery(id+"F6.imprint","IMPRINT",EDGE,{"derivedFrom":subQ1}),1.0]])]});}
            var Q22;
            {var subQ1=sQuery(id+"F6.wireOp",EDGE,"E203.MirrorCS");Q22=makeQuery(id+"F6.imprint","IMPRINT",FACE,{"disambiguationData":[TD([[makeQuery(id+"F6.imprint","IMPRINT",EDGE,{"derivedFrom":subQ1}),-1.0]])]});}
            var Q23;
            {var subQ1=sQuery(id+"F6.wireOp",EDGE,"E206.MirrorCS");Q23=makeQuery(id+"F6.imprint","IMPRINT",FACE,{"disambiguationData":[TD([[makeQuery(id+"F6.imprint","IMPRINT",EDGE,{"derivedFrom":subQ1}),-1.0]])]});}
            var Q24;
            {var subQ1=sQuery(id+"F6.wireOp",EDGE,"E205.MirrorCS");Q24=makeQuery(id+"F6.imprint","IMPRINT",FACE,{"disambiguationData":[TD([[makeQuery(id+"F6.imprint","IMPRINT",EDGE,{"derivedFrom":subQ1}),-1.0]])]});}
            var Q25;
            {var subQ1=sQuery(id+"F6.wireOp",EDGE,"E202.MirrorCS");Q25=makeQuery(id+"F6.imprint","IMPRINT",FACE,{"disambiguationData":[TD([[makeQuery(id+"F6.imprint","IMPRINT",EDGE,{"derivedFrom":subQ1}),-1.0]])]});}
            var Q26;
            {var subQ3=sQuery(id+"F6.wireOp",EDGE,"E190.MirrorCS");Q26=makeQuery(id+"F6.imprint","IMPRINT",FACE,{"disambiguationData":[TD([[makeQuery(id+"F6.imprint","IMPRINT",EDGE,{"derivedFrom":subQ3}),-1.0]])]});}
            var Q27;
            {var subQ1=sQuery(id+"F6.wireOp",EDGE,"E192.MirrorCS");Q27=makeQuery(id+"F6.imprint","IMPRINT",FACE,{"disambiguationData":[TD([[makeQuery(id+"F6.imprint","IMPRINT",EDGE,{"derivedFrom":subQ1}),-1.0]])]});}
            var Q28;
            {var subQ1=sQuery(id+"F6.wireOp",EDGE,"E200.MirrorCS");Q28=makeQuery(id+"F6.imprint","IMPRINT",FACE,{"disambiguationData":[TD([[makeQuery(id+"F6.imprint","IMPRINT",EDGE,{"derivedFrom":subQ1}),-1.0]])]});}
            extrude(context, id + "F7", {"entities" : qUnion([Q0, Q1, Q2, Q3, Q4, Q5, Q6, Q7, Q8, Q9, Q10, Q11, Q12, Q13, Q14, Q15, Q16, Q17, Q18, Q19, Q20, Q21, Q22, Q23, Q24, Q25, Q26, Q27, Q28]), "operationType" : NewBodyOperationType.REMOVE, "depth" : 25 * mm, "offsetDistance" : 25 * mm});
        }
    });
